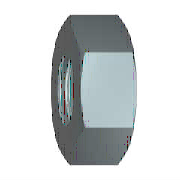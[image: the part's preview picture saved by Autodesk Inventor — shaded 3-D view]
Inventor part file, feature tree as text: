
AUTODESK INVENTOR PART (.ipt)
format: ipt  version: 2023 (Build 270158000, 158)  size: 164,864 bytes
history: native  units: mm (DEFAULTED — no unit token found)
features: sketch x3, other x2, extrude x1, hole x1, plane x1
ambient origin geometry x7: Origin, YZ Plane, XZ Plane, X Axis, Y Axis, Z Axis, Center Point
bodies: Solid1 (feature_tree)
feature tree (8):
  extrude  "Базовый элемент"  Depth=27.712813mm
  other  "Фаска1"
  hole  "Резьба"  [1 undecoded]
  other  "Work Axis1"
  plane  "Work Plane1"
  sketch  "Эскиз1"
  sketch  "Эскиз2"
  sketch  "Эскиз3"
note: 1 required parameter value undecoded (feature->parameter linkage not recoverable at this tier; creation-order binding heuristic only, values carry confidence <= 0.55)
